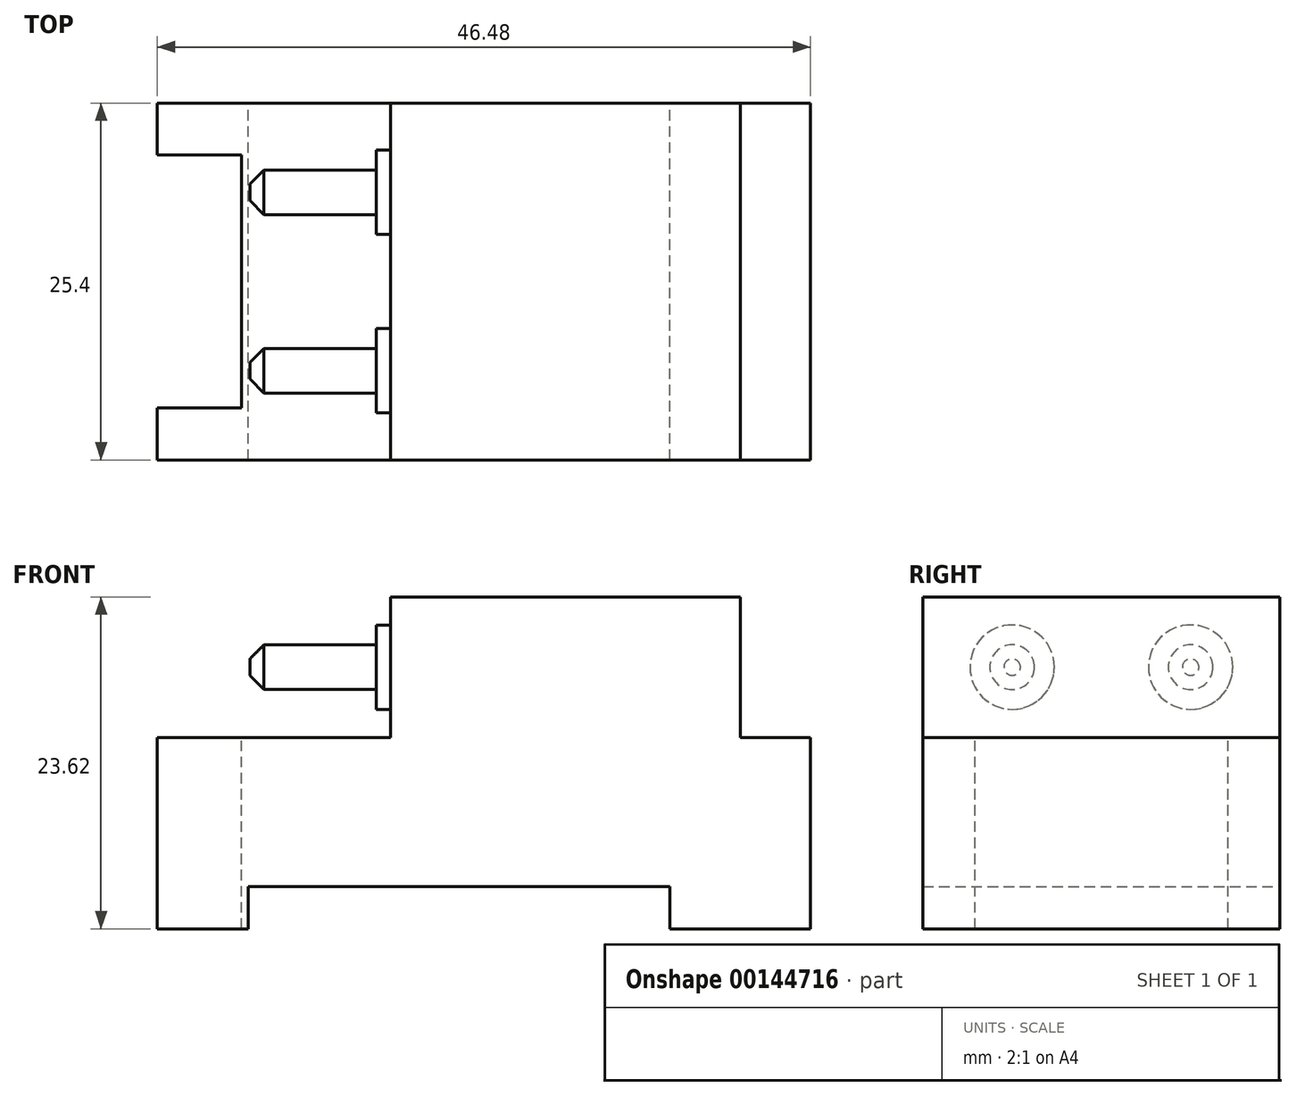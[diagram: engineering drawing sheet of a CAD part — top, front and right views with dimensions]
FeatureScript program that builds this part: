
annotation { "Feature Type Name" : "Feature", "Feature Type Description" : "" }
export const myFeature = defineFeature(function(context is Context, id is Id, definition is map)
    precondition{}
    {
        {
            var Q0;
            Q0=qCreatedBy(makeId("Top.planeOp"),FACE);
            var sketch = newSketch(context, id + "F0", { "sketchPlane" : qUnion([Q0])});
            skLineSegment(sketch, "E0.bottom", {"start": v(23.24, 12.7) * mm, "end": v(-23.24, 12.7) * mm});
            skLineSegment(sketch, "E0.top", {"start": v(23.24, -12.7) * mm, "end": v(-23.24, -12.7) * mm});
            skLineSegment(sketch, "E0.left", {"start": v(23.24, 12.7) * mm, "end": v(23.24, -12.7) * mm});
            skLineSegment(sketch, "E0.right", {"start": v(-23.24, 12.7) * mm, "end": v(-23.24, -12.7) * mm});
            skPoint(sketch, "E0.middle", {"position": v(0, 0) * mm});
            skSolve(sketch);
        }
        {
            var Q0;
            Q0 = qSketchRegion(id + "F0", true);
            extrude(context, id + "F1", {"entities" : qUnion([Q0]), "depth" : 23.62 * mm});
        }
        {
            var Q0;
            Q0=makeQuery(id+"F1.opExtrude","CAP_FACE",FACE,{"disambiguationData":[OSD([sQuery(id+"F0.wireOp",EDGE,"E0.bottom"),sQuery(id+"F0.wireOp",EDGE,"E0.top"),sQuery(id+"F0.wireOp",EDGE,"E0.left"),sQuery(id+"F0.wireOp",EDGE,"E0.right")])],"isStart":false});
            var sketch = newSketch(context, id + "F2", { "sketchPlane" : qUnion([Q0])});
            skLineSegment(sketch, "E1.left", {"start": v(18.24, -12.7) * mm, "end": v(18.24, 12.7) * mm});
            skLineSegment(sketch, "E1.right", {"start": v(-6.65, -12.7) * mm, "end": v(-6.65, 12.7) * mm});
            skPoint(sketch, "E1.middle", {"position": v(5.8, 0) * mm});
            skLineSegment(sketch, "E2.0.0", {"start": v(23.24, -12.7) * mm, "end": v(23.24, 12.7) * mm});
            skLineSegment(sketch, "E2.0.1", {"start": v(23.24, 12.7) * mm, "end": v(18.24, 12.7) * mm});
            skLineSegment(sketch, "E2.0.2", {"start": v(-23.24, 12.7) * mm, "end": v(-23.24, -12.7) * mm});
            skLineSegment(sketch, "E2.0.3", {"start": v(-23.24, -12.7) * mm, "end": v(23.24, -12.7) * mm});
            skLineSegment(sketch, "E3.trimOffspring", {"start": v(-6.65, 12.7) * mm, "end": v(-23.24, 12.7) * mm});
            skSolve(sketch);
        }
        {
            var Q0;
            Q0 = qSketchRegion(id + "F2", true);
            extrude(context, id + "F3", {"entities" : qUnion([Q0]), "operationType" : NewBodyOperationType.REMOVE, "oppositeDirection" : true, "depth" : 10 * mm});
        }
        {
            var Q0;
            Q0=makeQuery(id+"F3.boolean.opBoolean","COPY",FACE,{"derivedFrom":makeQuery(id+"F3.opExtrude","CAP_FACE",FACE,{"disambiguationData":[OSD([sQuery(id+"F2.wireOp",EDGE,"E1.right"),sQuery(id+"F2.wireOp",EDGE,"E2.0.2"),sQuery(id+"F2.wireOp",EDGE,"E2.0.3"),sQuery(id+"F2.wireOp",EDGE,"E3.trimOffspring")])],"isStart":false})});
            var sketch = newSketch(context, id + "F4", { "sketchPlane" : qUnion([Q0])});
            skLineSegment(sketch, "E4.bottom", {"start": v(-23.24, -9) * mm, "end": v(-17.24, -9) * mm});
            skLineSegment(sketch, "E4.top", {"start": v(-23.24, 9) * mm, "end": v(-17.24, 9) * mm});
            skLineSegment(sketch, "E4.left", {"start": v(-23.24, -9) * mm, "end": v(-23.24, 9) * mm});
            skLineSegment(sketch, "E4.right", {"start": v(-17.24, -9) * mm, "end": v(-17.24, 9) * mm});
            skPoint(sketch, "E4.middle", {"position": v(-20.24, 0) * mm});
            skSolve(sketch);
        }
        {
            var Q0;
            Q0 = qSketchRegion(id + "F4", true);
            extrude(context, id + "F5", {"entities" : qUnion([Q0]), "operationType" : NewBodyOperationType.REMOVE, "endBound" : BoundingType.THROUGH_ALL, "oppositeDirection" : true, "depth" : 25.4 * mm});
        }
        {
            var Q0;
            Q0=makeQuery(id+"F1.opExtrude","SWEPT_FACE",FACE,{"disambiguationData":[OSD([sQuery(id+"F0.wireOp",EDGE,"E0.bottom")])]});
            var sketch = newSketch(context, id + "F6", { "sketchPlane" : qUnion([Q0])});
            skLineSegment(sketch, "E5.bottom", {"start": v(-13.24, 0) * mm, "end": v(16.76, 0) * mm});
            skLineSegment(sketch, "E5.top", {"start": v(-13.24, 3) * mm, "end": v(16.76, 3) * mm});
            skLineSegment(sketch, "E5.left", {"start": v(-13.24, 0) * mm, "end": v(-13.24, 3) * mm});
            skLineSegment(sketch, "E5.right", {"start": v(16.76, 0) * mm, "end": v(16.76, 3) * mm});
            skSolve(sketch);
        }
        {
            var Q0;
            Q0 = qSketchRegion(id + "F6", true);
            extrude(context, id + "F7", {"entities" : qUnion([Q0]), "operationType" : NewBodyOperationType.REMOVE, "endBound" : BoundingType.THROUGH_ALL, "oppositeDirection" : true, "depth" : 25.4 * mm});
        }
        {
            var Q0;
            Q0=makeQuery(id+"F3.boolean.opBoolean","COPY",FACE,{"derivedFrom":makeQuery(id+"F3.opExtrude","SWEPT_FACE",FACE,{"disambiguationData":[OSD([sQuery(id+"F2.wireOp",EDGE,"E1.right")])]})});
            var sketch = newSketch(context, id + "F8", { "sketchPlane" : qUnion([Q0])});
            skLineSegment(sketch, "E6.0.0", {"start": v(12.7, 23.62) * mm, "end": v(-12.7, 23.62) * mm, "construction": true});
            skLineSegment(sketch, "E6.0.1", {"start": v(-12.7, 23.62) * mm, "end": v(-12.7, 13.62) * mm, "construction": true});
            skLineSegment(sketch, "E6.0.2", {"start": v(-12.7, 13.62) * mm, "end": v(12.7, 13.62) * mm, "construction": true});
            skLineSegment(sketch, "E6.0.3", {"start": v(12.7, 13.62) * mm, "end": v(12.7, 23.62) * mm, "construction": true});
            skLineSegment(sketch, "E7", {"start": v(-12.7, 18.62) * mm, "end": v(0, 18.62) * mm, "construction": true});
            skLineSegment(sketch, "E8", {"start": v(0, 23.62) * mm, "end": v(0, 13.62) * mm, "construction": true});
            skPoint(sketch, "E9", {"position": v(-6.35, 18.62) * mm});
            skPoint(sketch, "E10", {"position": v(6.35, 18.62) * mm});
            skPoint(sketch, "E11.trimOffspring.end.orphan", {"position": v(12.7, 18.62) * mm});
            skCircle(sketch, "E12", {"center": v(-6.35, 18.62) * mm, "radius": 1.59 * mm});
            skCircle(sketch, "E13", {"center": v(6.35, 18.62) * mm, "radius": 1.59 * mm});
            skSolve(sketch);
        }
        {
            var Q0;
            Q0 = qSketchRegion(id + "F8", true);
            extrude(context, id + "F9", {"entities" : qUnion([Q0]), "operationType" : NewBodyOperationType.ADD, "depth" : 10 * mm});
        }
        {
            var Q0;
            Q0=makeQuery(id+"F3.boolean.opBoolean","COPY",FACE,{"derivedFrom":makeQuery(id+"F3.opExtrude","SWEPT_FACE",FACE,{"disambiguationData":[OSD([sQuery(id+"F2.wireOp",EDGE,"E1.right")])]})});
            var sketch = newSketch(context, id + "F10", { "sketchPlane" : qUnion([Q0])});
            skCircle(sketch, "E14", {"center": v(-6.35, 18.62) * mm, "radius": 3 * mm});
            skCircle(sketch, "E15", {"center": v(6.35, 18.62) * mm, "radius": 3 * mm});
            skSolve(sketch);
        }
        {
            var Q0;
            Q0 = qSketchRegion(id + "F10", true);
            extrude(context, id + "F11", {"entities" : qUnion([Q0]), "operationType" : NewBodyOperationType.ADD, "depth" : 1 * mm});
        }
        {
            var Q0;
            Q0=makeQuery(id+"F9.opExtrude","CAP_EDGE",EDGE,{"disambiguationData":[OSD([sQuery(id+"F8.wireOp",EDGE,"E12")])],"isStart":false});
            var Q1;
            Q1=makeQuery(id+"F9.opExtrude","CAP_EDGE",EDGE,{"disambiguationData":[OSD([sQuery(id+"F8.wireOp",EDGE,"E13")])],"isStart":false});
            chamfer(context, id + "F12", {"entities" : qUnion([Q0, Q1]), "width" : 1 * mm, "tangentPropagation" : true});
        }
    });
